# Revit family: 859-002X-001 DN350-600
name_source: partatom
category: Pipe Accessories
units: mm (PartAtom-declared; Revit-internal decimal feet)

## family parameters
Always vertical = Yes
Cut with Voids When Loaded = No
Part Type = Valve - Breaks Into
Round Connector Dimension = Use Diameter
Shared = No
Work Plane-Based = No

## types (40) — shared parameters
10 = 10 mm  [stored 0.0328084 ft]
18 = 11 mm  [stored 0.0360892 ft]
3 = 3 mm  [stored 0.00984252 ft]
50 = 50 mm
8 = 8 mm  [stored 0.0262467 ft]
DN350_PN10 Flow range ( 170 - 420) = 859-0350-00-0140020
DN350_PN10 Flow range ( 225 - 555) = 859-0350-00-0140021
DN350_PN10 Flow range ( 510 - 1250) = 859-0350-00-0140022
DN350_PN10 Flow range ( 650 - 1595) = 859-0350-00-0140023
DN350_PN16 Flow range ( 170 - 420) = 859-0350-00-1140020
DN350_PN16 Flow range ( 225 - 555) = 859-0350-00-1140021
859-0350-00-1140021
859-0350-00-1140021
859-0350-00-1140021
DN350_PN16 Flow range ( 510 - 1250) = 859-0350-00-1140022
DN350_PN16 Flow range ( 650 - 1595) = 859-0350-00-1140023
DN400_PN10 Flow range ( 225 - 545) = 859-0400-00-0140020
DN400_PN10 Flow range ( 370 - 905) = 859-0400-00-0140021
DN400_PN10 Flow range ( 525 - 1285) = 859-0400-00-0140022
DN400_PN10 Flow range ( 740 - 1815) = 859-0400-00-0140023
DN400_PN16 Flow range ( 225 - 545) = 859-0400-00-1140020
DN400_PN16 Flow range ( 370 - 905) = 859-0400-00-1140021
DN400_PN16 Flow range ( 525 - 1285) = 859-0400-00-1140022
DN400_PN16 Flow range ( 740 - 1815) = 859-0400-00-1140023
DN450_PN10 Flow range ( 1020 - 2495) = 859-0450-00-0140023
DN450_PN10 Flow range ( 280 - 690) = 859-0450-00-0140020
DN450_PN10 Flow range ( 445 - 1090) = 859-0450-00-0140021
DN450_PN10 Flow range ( 675 - 1640) = 859-0450-00-0140022
DN450_PN16 Flow range ( 1020 - 2495) = 859-0450-00-1140023
DN450_PN16 Flow range ( 280 - 690) = 859-0450-00-1140020
DN450_PN16 Flow range ( 445 - 1090) = 859-0450-00-1140021
DN450_PN16 Flow range ( 675 - 1640) = 859-0450-00-1140022
DN500_PN10 Flow range ( 1115 - 2715) = 859-0500-00-0140023
DN500_PN10 Flow range ( 350 - 835) = 859-0500-00-0140020
DN500_PN10 Flow range ( 530 - 1290) = 859-0500-00-0140021
DN500_PN10 Flow range ( 765 - 1860) = 859-0500-00-0140022
DN500_PN16 Flow range ( 1115 - 2715) = 859-0500-00-1140023
DN500_PN16 Flow range ( 350 - 835) = 859-0500-00-1140020
DN500_PN16 Flow range ( 530 - 1290) = 859-0500-00-1140021
DN500_PN16 Flow range ( 765 - 1860) = 859-0500-00-1140022
DN600_PN10 Flow range ( 1780 - 4350) = 859-0600-00-0140023
DN600_PN10 Flow range ( 500 - 1225) = 859-0600-00-0140020
DN600_PN10 Flow range ( 710 - 1735) = 859-0600-00-0140021
DN600_PN10 Flow range ( 970 - 2360) = 859-0600-00-0140022
DN600_PN16 Flow range ( 1780 - 4350) = 859-0600-00-1140023
DN600_PN16 Flow range ( 500 - 1225) = 859-0600-00-1140020
DN600_PN16 Flow range ( 710 - 1735) = 859-0600-00-1140021
DN600_PN16 Flow range ( 970 - 2360) = 859-0600-00-1140022
Description_ = AVK CONTROL VALVE, CONSTANT FLOW, PN10/16
Orifice_FL_T = 14 mm  [stored 0.0459318 ft]
Search_table = 859-002X-001 DN350-600
URL_product_pages = https://www.avkvalves.com
zero-valued in all types: 0, Default Elevation

## per-type parameters (varying)
- DN350_PN10 Flow range ( 170 - 420): Actuator_L=136 mm; Actuator_L1=122 mm; Actuator_d=41 mm; Body_H=312 mm; Body_Rib_L=130 mm; Bolt_Dia=33 mm; Bonnet_D=156 mm; Bonnet_D1=312 mm; Bonnet_R=328 mm; Bonnet_dim1=218 mm; Bonnet_dim1_H=32 mm; Bonnet_dim1_H1=431 mm; Bonnet_dim2=109 mm; Bonnet_dim3=82 mm; Bore=175 mm; Bore1=210 mm; Bore2=280 mm; Centre_D=90 mm; Centre_D1=72 mm; Centre_nut=68 mm; Control_dim1=16 mm  [stored 0.0524934 ft]; Control_dim2=98 mm; Control_dim3=8 mm  [stored 0.0262467 ft]; Control_dim4=281 mm; Control_dim5=22 mm; Control_dim6=27 mm; Control_dim7=48 mm; D=260 mm; DN=350 mm; FL_T=27 mm; H3=796 mm; H33=99 mm; H4=199 mm; L=980 mm; L3=360 mm; Nut_Dim1=42 mm; Nut_Dim2=7 mm  [stored 0.0229659 ft]; Nut_T=21 mm; Orifice_FL=219 mm; Raised_R=34 mm  [stored 0.111549 ft]; Raised_dis=4 mm  [stored 0.0131234 ft]; Sweep_R=19 mm  [stored 0.062336 ft]; Thickness=16 mm  [stored 0.0524934 ft]; Thickness1=19 mm  [stored 0.062336 ft]; Total_L=995 mm; W=290 mm; W1=302 mm; W11=208 mm; W2=302 mm; W22=242 mm; centre=273 mm; dim1=91 mm; nut_dim=156 mm; sweep=30 mm  [stored 0.0984252 ft]; sweep/2=6 mm  [stored 0.019685 ft]; sweep1=13 mm  [stored 0.0426509 ft]; sweep_D=25 mm  [stored 0.082021 ft]; sweep_H=375 mm; sweep_H1=44 mm; sweep_box1=36 mm  [stored 0.11811 ft]; sweep_box2=16 mm  [stored 0.0524934 ft]; w1=302 mm; w2=302 mm
- DN350_PN10 Flow range ( 225 - 555): Actuator_L=136 mm; Actuator_L1=122 mm; Actuator_d=41 mm; Body_H=312 mm; Body_Rib_L=130 mm; Bolt_Dia=33 mm; Bonnet_D=156 mm; Bonnet_D1=312 mm; Bonnet_R=328 mm; Bonnet_dim1=218 mm; Bonnet_dim1_H=32 mm; Bonnet_dim1_H1=431 mm; Bonnet_dim2=109 mm; Bonnet_dim3=82 mm; Bore=175 mm; Bore1=210 mm; Bore2=280 mm; Centre_D=90 mm; Centre_D1=72 mm; Centre_nut=68 mm; Control_dim1=16 mm  [stored 0.0524934 ft]; Control_dim2=98 mm; Control_dim3=8 mm  [stored 0.0262467 ft]; Control_dim4=281 mm; Control_dim5=22 mm; Control_dim6=27 mm; Control_dim7=48 mm; D=260 mm; DN=350 mm; FL_T=27 mm; H3=796 mm; H33=99 mm; H4=199 mm; L=980 mm; L3=360 mm; Nut_Dim1=42 mm; Nut_Dim2=7 mm  [stored 0.0229659 ft]; Nut_T=21 mm; Orifice_FL=219 mm; Raised_R=34 mm  [stored 0.111549 ft]; Raised_dis=4 mm  [stored 0.0131234 ft]; Sweep_R=19 mm  [stored 0.062336 ft]; Thickness=16 mm  [stored 0.0524934 ft]; Thickness1=19 mm  [stored 0.062336 ft]; Total_L=995 mm; W=290 mm; W1=302 mm; W11=208 mm; W2=302 mm; W22=242 mm; centre=273 mm; dim1=91 mm; nut_dim=156 mm; sweep=30 mm  [stored 0.0984252 ft]; sweep/2=6 mm  [stored 0.019685 ft]; sweep1=13 mm  [stored 0.0426509 ft]; sweep_D=25 mm  [stored 0.082021 ft]; sweep_H=375 mm; sweep_H1=44 mm; sweep_box1=36 mm  [stored 0.11811 ft]; sweep_box2=16 mm  [stored 0.0524934 ft]; w1=302 mm; w2=302 mm
- DN350_PN10 Flow range ( 510 - 1250): Actuator_L=136 mm; Actuator_L1=122 mm; Actuator_d=41 mm; Body_H=312 mm; Body_Rib_L=130 mm; Bolt_Dia=33 mm; Bonnet_D=156 mm; Bonnet_D1=312 mm; Bonnet_R=328 mm; Bonnet_dim1=218 mm; Bonnet_dim1_H=32 mm; Bonnet_dim1_H1=431 mm; Bonnet_dim2=109 mm; Bonnet_dim3=82 mm; Bore=175 mm; Bore1=210 mm; Bore2=280 mm; Centre_D=90 mm; Centre_D1=72 mm; Centre_nut=68 mm; Control_dim1=16 mm  [stored 0.0524934 ft]; Control_dim2=98 mm; Control_dim3=8 mm  [stored 0.0262467 ft]; Control_dim4=281 mm; Control_dim5=22 mm; Control_dim6=27 mm; Control_dim7=48 mm; D=260 mm; DN=350 mm; FL_T=27 mm; H3=796 mm; H33=99 mm; H4=199 mm; L=980 mm; L3=360 mm; Nut_Dim1=42 mm; Nut_Dim2=7 mm  [stored 0.0229659 ft]; Nut_T=21 mm; Orifice_FL=219 mm; Raised_R=34 mm  [stored 0.111549 ft]; Raised_dis=4 mm  [stored 0.0131234 ft]; Sweep_R=19 mm  [stored 0.062336 ft]; Thickness=16 mm  [stored 0.0524934 ft]; Thickness1=19 mm  [stored 0.062336 ft]; Total_L=995 mm; W=290 mm; W1=302 mm; W11=208 mm; W2=302 mm; W22=242 mm; centre=273 mm; dim1=91 mm; nut_dim=156 mm; sweep=30 mm  [stored 0.0984252 ft]; sweep/2=6 mm  [stored 0.019685 ft]; sweep1=13 mm  [stored 0.0426509 ft]; sweep_D=25 mm  [stored 0.082021 ft]; sweep_H=375 mm; sweep_H1=44 mm; sweep_box1=36 mm  [stored 0.11811 ft]; sweep_box2=16 mm  [stored 0.0524934 ft]; w1=302 mm; w2=302 mm
- DN350_PN10 Flow range ( 650 - 1595): Actuator_L=136 mm; Actuator_L1=122 mm; Actuator_d=41 mm; Body_H=312 mm; Body_Rib_L=130 mm; Bolt_Dia=33 mm; Bonnet_D=156 mm; Bonnet_D1=312 mm; Bonnet_R=328 mm; Bonnet_dim1=218 mm; Bonnet_dim1_H=32 mm; Bonnet_dim1_H1=431 mm; Bonnet_dim2=109 mm; Bonnet_dim3=82 mm; Bore=175 mm; Bore1=210 mm; Bore2=280 mm; Centre_D=90 mm; Centre_D1=72 mm; Centre_nut=68 mm; Control_dim1=16 mm  [stored 0.0524934 ft]; Control_dim2=98 mm; Control_dim3=8 mm  [stored 0.0262467 ft]; Control_dim4=281 mm; Control_dim5=22 mm; Control_dim6=27 mm; Control_dim7=48 mm; D=260 mm; DN=350 mm; FL_T=27 mm; H3=796 mm; H33=99 mm; H4=199 mm; L=980 mm; L3=360 mm; Nut_Dim1=42 mm; Nut_Dim2=7 mm  [stored 0.0229659 ft]; Nut_T=21 mm; Orifice_FL=219 mm; Raised_R=34 mm  [stored 0.111549 ft]; Raised_dis=4 mm  [stored 0.0131234 ft]; Sweep_R=19 mm  [stored 0.062336 ft]; Thickness=16 mm  [stored 0.0524934 ft]; Thickness1=19 mm  [stored 0.062336 ft]; Total_L=995 mm; W=290 mm; W1=302 mm; W11=208 mm; W2=302 mm; W22=242 mm; centre=273 mm; dim1=91 mm; nut_dim=156 mm; sweep=30 mm  [stored 0.0984252 ft]; sweep/2=6 mm  [stored 0.019685 ft]; sweep1=13 mm  [stored 0.0426509 ft]; sweep_D=25 mm  [stored 0.082021 ft]; sweep_H=375 mm; sweep_H1=44 mm; sweep_box1=36 mm  [stored 0.11811 ft]; sweep_box2=16 mm  [stored 0.0524934 ft]; w1=302 mm; w2=302 mm
- DN350_PN16 Flow range ( 170 - 420): Actuator_L=136 mm; Actuator_L1=122 mm; Actuator_d=41 mm; Body_H=312 mm; Body_Rib_L=130 mm; Bolt_Dia=33 mm; Bonnet_D=156 mm; Bonnet_D1=312 mm; Bonnet_R=328 mm; Bonnet_dim1=218 mm; Bonnet_dim1_H=32 mm; Bonnet_dim1_H1=431 mm; Bonnet_dim2=109 mm; Bonnet_dim3=82 mm; Bore=175 mm; Bore1=210 mm; Bore2=280 mm; Centre_D=90 mm; Centre_D1=72 mm; Centre_nut=68 mm; Control_dim1=16 mm  [stored 0.0524934 ft]; Control_dim2=98 mm; Control_dim3=8 mm  [stored 0.0262467 ft]; Control_dim4=281 mm; Control_dim5=22 mm; Control_dim6=27 mm; Control_dim7=48 mm; D=260 mm; DN=350 mm; FL_T=27 mm; H3=796 mm; H33=99 mm; H4=199 mm; L=980 mm; L3=360 mm; Nut_Dim1=42 mm; Nut_Dim2=7 mm  [stored 0.0229659 ft]; Nut_T=21 mm; Orifice_FL=219 mm; Raised_R=34 mm  [stored 0.111549 ft]; Raised_dis=4 mm  [stored 0.0131234 ft]; Sweep_R=19 mm  [stored 0.062336 ft]; Thickness=16 mm  [stored 0.0524934 ft]; Thickness1=19 mm  [stored 0.062336 ft]; Total_L=995 mm; W=290 mm; W1=302 mm; W11=208 mm; W2=302 mm; W22=242 mm; centre=273 mm; dim1=91 mm; nut_dim=156 mm; sweep=30 mm  [stored 0.0984252 ft]; sweep/2=6 mm  [stored 0.019685 ft]; sweep1=13 mm  [stored 0.0426509 ft]; sweep_D=25 mm  [stored 0.082021 ft]; sweep_H=375 mm; sweep_H1=44 mm; sweep_box1=36 mm  [stored 0.11811 ft]; sweep_box2=16 mm  [stored 0.0524934 ft]; w1=302 mm; w2=302 mm
- DN350_PN16 Flow range ( 225 - 555): Actuator_L=136 mm; Actuator_L1=122 mm; Actuator_d=41 mm; Body_H=312 mm; Body_Rib_L=130 mm; Bolt_Dia=33 mm; Bonnet_D=156 mm; Bonnet_D1=312 mm; Bonnet_R=328 mm; Bonnet_dim1=218 mm; Bonnet_dim1_H=32 mm; Bonnet_dim1_H1=431 mm; Bonnet_dim2=109 mm; Bonnet_dim3=82 mm; Bore=175 mm; Bore1=210 mm; Bore2=280 mm; Centre_D=90 mm; Centre_D1=72 mm; Centre_nut=68 mm; Control_dim1=16 mm  [stored 0.0524934 ft]; Control_dim2=98 mm; Control_dim3=8 mm  [stored 0.0262467 ft]; Control_dim4=281 mm; Control_dim5=22 mm; Control_dim6=27 mm; Control_dim7=48 mm; D=260 mm; DN=350 mm; FL_T=27 mm; H3=796 mm; H33=99 mm; H4=199 mm; L=980 mm; L3=360 mm; Nut_Dim1=42 mm; Nut_Dim2=7 mm  [stored 0.0229659 ft]; Nut_T=21 mm; Orifice_FL=219 mm; Raised_R=34 mm  [stored 0.111549 ft]; Raised_dis=4 mm  [stored 0.0131234 ft]; Sweep_R=19 mm  [stored 0.062336 ft]; Thickness=16 mm  [stored 0.0524934 ft]; Thickness1=19 mm  [stored 0.062336 ft]; Total_L=995 mm; W=290 mm; W1=302 mm; W11=208 mm; W2=302 mm; W22=242 mm; centre=273 mm; dim1=91 mm; nut_dim=156 mm; sweep=30 mm  [stored 0.0984252 ft]; sweep/2=6 mm  [stored 0.019685 ft]; sweep1=13 mm  [stored 0.0426509 ft]; sweep_D=25 mm  [stored 0.082021 ft]; sweep_H=375 mm; sweep_H1=44 mm; sweep_box1=36 mm  [stored 0.11811 ft]; sweep_box2=16 mm  [stored 0.0524934 ft]; w1=302 mm; w2=302 mm
- DN350_PN16 Flow range ( 510 - 1250): Actuator_L=136 mm; Actuator_L1=122 mm; Actuator_d=41 mm; Body_H=312 mm; Body_Rib_L=130 mm; Bolt_Dia=33 mm; Bonnet_D=156 mm; Bonnet_D1=312 mm; Bonnet_R=328 mm; Bonnet_dim1=218 mm; Bonnet_dim1_H=32 mm; Bonnet_dim1_H1=431 mm; Bonnet_dim2=109 mm; Bonnet_dim3=82 mm; Bore=175 mm; Bore1=210 mm; Bore2=280 mm; Centre_D=90 mm; Centre_D1=72 mm; Centre_nut=68 mm; Control_dim1=16 mm  [stored 0.0524934 ft]; Control_dim2=98 mm; Control_dim3=8 mm  [stored 0.0262467 ft]; Control_dim4=281 mm; Control_dim5=22 mm; Control_dim6=27 mm; Control_dim7=48 mm; D=260 mm; DN=350 mm; FL_T=27 mm; H3=796 mm; H33=99 mm; H4=199 mm; L=980 mm; L3=360 mm; Nut_Dim1=42 mm; Nut_Dim2=7 mm  [stored 0.0229659 ft]; Nut_T=21 mm; Orifice_FL=219 mm; Raised_R=34 mm  [stored 0.111549 ft]; Raised_dis=4 mm  [stored 0.0131234 ft]; Sweep_R=19 mm  [stored 0.062336 ft]; Thickness=16 mm  [stored 0.0524934 ft]; Thickness1=19 mm  [stored 0.062336 ft]; Total_L=995 mm; W=290 mm; W1=302 mm; W11=208 mm; W2=302 mm; W22=242 mm; centre=273 mm; dim1=91 mm; nut_dim=156 mm; sweep=30 mm  [stored 0.0984252 ft]; sweep/2=6 mm  [stored 0.019685 ft]; sweep1=13 mm  [stored 0.0426509 ft]; sweep_D=25 mm  [stored 0.082021 ft]; sweep_H=375 mm; sweep_H1=44 mm; sweep_box1=36 mm  [stored 0.11811 ft]; sweep_box2=16 mm  [stored 0.0524934 ft]; w1=302 mm; w2=302 mm
- DN350_PN16 Flow range ( 650 - 1595): Actuator_L=136 mm; Actuator_L1=122 mm; Actuator_d=41 mm; Body_H=312 mm; Body_Rib_L=130 mm; Bolt_Dia=33 mm; Bonnet_D=156 mm; Bonnet_D1=312 mm; Bonnet_R=328 mm; Bonnet_dim1=218 mm; Bonnet_dim1_H=32 mm; Bonnet_dim1_H1=431 mm; Bonnet_dim2=109 mm; Bonnet_dim3=82 mm; Bore=175 mm; Bore1=210 mm; Bore2=280 mm; Centre_D=90 mm; Centre_D1=72 mm; Centre_nut=68 mm; Control_dim1=16 mm  [stored 0.0524934 ft]; Control_dim2=98 mm; Control_dim3=8 mm  [stored 0.0262467 ft]; Control_dim4=281 mm; Control_dim5=22 mm; Control_dim6=27 mm; Control_dim7=48 mm; D=260 mm; DN=350 mm; FL_T=27 mm; H3=796 mm; H33=99 mm; H4=199 mm; L=980 mm; L3=360 mm; Nut_Dim1=42 mm; Nut_Dim2=7 mm  [stored 0.0229659 ft]; Nut_T=21 mm; Orifice_FL=219 mm; Raised_R=34 mm  [stored 0.111549 ft]; Raised_dis=4 mm  [stored 0.0131234 ft]; Sweep_R=19 mm  [stored 0.062336 ft]; Thickness=16 mm  [stored 0.0524934 ft]; Thickness1=19 mm  [stored 0.062336 ft]; Total_L=995 mm; W=290 mm; W1=302 mm; W11=208 mm; W2=302 mm; W22=242 mm; centre=273 mm; dim1=91 mm; nut_dim=156 mm; sweep=30 mm  [stored 0.0984252 ft]; sweep/2=6 mm  [stored 0.019685 ft]; sweep1=13 mm  [stored 0.0426509 ft]; sweep_D=25 mm  [stored 0.082021 ft]; sweep_H=375 mm; sweep_H1=44 mm; sweep_box1=36 mm  [stored 0.11811 ft]; sweep_box2=16 mm  [stored 0.0524934 ft]; w1=302 mm; w2=302 mm
- DN400_PN10 Flow range ( 225 - 545): Actuator_L=160 mm; Actuator_L1=144 mm; Actuator_d=45 mm  [stored 0.147638 ft]; Body_H=348 mm; Body_Rib_L=145 mm; Bolt_Dia=39 mm  [stored 0.127953 ft]; Bonnet_D=174 mm; Bonnet_D1=348 mm; Bonnet_R=365 mm; Bonnet_dim1=244 mm; Bonnet_dim1_H=47 mm; Bonnet_dim1_H1=507 mm; Bonnet_dim2=122 mm; Bonnet_dim3=91 mm; Bore=200 mm; Bore1=240 mm; Bore2=320 mm; Centre_D=90 mm; Centre_D1=72 mm; Centre_nut=68 mm; Control_dim1=18 mm  [stored 0.0590551 ft]; Control_dim2=110 mm; Control_dim3=9 mm  [stored 0.0295276 ft]; Control_dim4=313 mm; Control_dim5=25 mm  [stored 0.082021 ft]; Control_dim6=30 mm  [stored 0.0984252 ft]; Control_dim7=53 mm; D=290 mm; DN=400 mm; FL_T=28 mm  [stored 0.0918635 ft]; H3=920 mm; H33=117 mm; H4=233 mm; L=1100 mm; L3=402 mm; Nut_Dim1=51 mm; Nut_Dim2=7 mm  [stored 0.0229659 ft]; Nut_T=22 mm; Orifice_FL=244 mm; Raised_R=36 mm  [stored 0.11811 ft]; Raised_dis=4 mm  [stored 0.0131234 ft]; Sweep_R=23 mm; Thickness=17 mm; Thickness1=20 mm  [stored 0.0656168 ft]; Total_L=1115 mm; W=340 mm; W1=355 mm; W11=244 mm; W2=355 mm; W22=284 mm; centre=312 mm; dim1=107 mm; nut_dim=174 mm; sweep=36 mm  [stored 0.11811 ft]; sweep/2=8 mm  [stored 0.0262467 ft]; sweep1=15 mm  [stored 0.0492126 ft]; sweep_D=30 mm  [stored 0.0984252 ft]; sweep_H=441 mm; sweep_H1=65 mm; sweep_box1=36 mm  [stored 0.11811 ft]; sweep_box2=20 mm  [stored 0.0656168 ft]; w1=355 mm; w2=355 mm
- DN400_PN10 Flow range ( 370 - 905): Actuator_L=160 mm; Actuator_L1=144 mm; Actuator_d=45 mm  [stored 0.147638 ft]; Body_H=348 mm; Body_Rib_L=145 mm; Bolt_Dia=39 mm  [stored 0.127953 ft]; Bonnet_D=174 mm; Bonnet_D1=348 mm; Bonnet_R=365 mm; Bonnet_dim1=244 mm; Bonnet_dim1_H=47 mm; Bonnet_dim1_H1=507 mm; Bonnet_dim2=122 mm; Bonnet_dim3=91 mm; Bore=200 mm; Bore1=240 mm; Bore2=320 mm; Centre_D=90 mm; Centre_D1=72 mm; Centre_nut=68 mm; Control_dim1=18 mm  [stored 0.0590551 ft]; Control_dim2=110 mm; Control_dim3=9 mm  [stored 0.0295276 ft]; Control_dim4=313 mm; Control_dim5=25 mm  [stored 0.082021 ft]; Control_dim6=30 mm  [stored 0.0984252 ft]; Control_dim7=53 mm; D=290 mm; DN=400 mm; FL_T=28 mm  [stored 0.0918635 ft]; H3=920 mm; H33=117 mm; H4=233 mm; L=1100 mm; L3=402 mm; Nut_Dim1=51 mm; Nut_Dim2=7 mm  [stored 0.0229659 ft]; Nut_T=22 mm; Orifice_FL=244 mm; Raised_R=36 mm  [stored 0.11811 ft]; Raised_dis=4 mm  [stored 0.0131234 ft]; Sweep_R=23 mm; Thickness=17 mm; Thickness1=20 mm  [stored 0.0656168 ft]; Total_L=1115 mm; W=340 mm; W1=355 mm; W11=244 mm; W2=355 mm; W22=284 mm; centre=312 mm; dim1=107 mm; nut_dim=174 mm; sweep=36 mm  [stored 0.11811 ft]; sweep/2=8 mm  [stored 0.0262467 ft]; sweep1=15 mm  [stored 0.0492126 ft]; sweep_D=30 mm  [stored 0.0984252 ft]; sweep_H=441 mm; sweep_H1=65 mm; sweep_box1=36 mm  [stored 0.11811 ft]; sweep_box2=20 mm  [stored 0.0656168 ft]; w1=355 mm; w2=355 mm
- DN400_PN10 Flow range ( 525 - 1285): Actuator_L=160 mm; Actuator_L1=144 mm; Actuator_d=45 mm  [stored 0.147638 ft]; Body_H=348 mm; Body_Rib_L=145 mm; Bolt_Dia=39 mm  [stored 0.127953 ft]; Bonnet_D=174 mm; Bonnet_D1=348 mm; Bonnet_R=365 mm; Bonnet_dim1=244 mm; Bonnet_dim1_H=47 mm; Bonnet_dim1_H1=507 mm; Bonnet_dim2=122 mm; Bonnet_dim3=91 mm; Bore=200 mm; Bore1=240 mm; Bore2=320 mm; Centre_D=90 mm; Centre_D1=72 mm; Centre_nut=68 mm; Control_dim1=18 mm  [stored 0.0590551 ft]; Control_dim2=110 mm; Control_dim3=9 mm  [stored 0.0295276 ft]; Control_dim4=313 mm; Control_dim5=25 mm  [stored 0.082021 ft]; Control_dim6=30 mm  [stored 0.0984252 ft]; Control_dim7=53 mm; D=290 mm; DN=400 mm; FL_T=28 mm  [stored 0.0918635 ft]; H3=920 mm; H33=117 mm; H4=233 mm; L=1100 mm; L3=402 mm; Nut_Dim1=51 mm; Nut_Dim2=7 mm  [stored 0.0229659 ft]; Nut_T=22 mm; Orifice_FL=244 mm; Raised_R=36 mm  [stored 0.11811 ft]; Raised_dis=4 mm  [stored 0.0131234 ft]; Sweep_R=23 mm; Thickness=17 mm; Thickness1=20 mm  [stored 0.0656168 ft]; Total_L=1115 mm; W=340 mm; W1=355 mm; W11=244 mm; W2=355 mm; W22=284 mm; centre=312 mm; dim1=107 mm; nut_dim=174 mm; sweep=36 mm  [stored 0.11811 ft]; sweep/2=8 mm  [stored 0.0262467 ft]; sweep1=15 mm  [stored 0.0492126 ft]; sweep_D=30 mm  [stored 0.0984252 ft]; sweep_H=441 mm; sweep_H1=65 mm; sweep_box1=36 mm  [stored 0.11811 ft]; sweep_box2=20 mm  [stored 0.0656168 ft]; w1=355 mm; w2=355 mm
- DN400_PN10 Flow range ( 740 - 1815): Actuator_L=160 mm; Actuator_L1=144 mm; Actuator_d=45 mm  [stored 0.147638 ft]; Body_H=348 mm; Body_Rib_L=145 mm; Bolt_Dia=39 mm  [stored 0.127953 ft]; Bonnet_D=174 mm; Bonnet_D1=348 mm; Bonnet_R=365 mm; Bonnet_dim1=244 mm; Bonnet_dim1_H=47 mm; Bonnet_dim1_H1=507 mm; Bonnet_dim2=122 mm; Bonnet_dim3=91 mm; Bore=200 mm; Bore1=240 mm; Bore2=320 mm; Centre_D=90 mm; Centre_D1=72 mm; Centre_nut=68 mm; Control_dim1=18 mm  [stored 0.0590551 ft]; Control_dim2=110 mm; Control_dim3=9 mm  [stored 0.0295276 ft]; Control_dim4=313 mm; Control_dim5=25 mm  [stored 0.082021 ft]; Control_dim6=30 mm  [stored 0.0984252 ft]; Control_dim7=53 mm; D=290 mm; DN=400 mm; FL_T=28 mm  [stored 0.0918635 ft]; H3=920 mm; H33=117 mm; H4=233 mm; L=1100 mm; L3=402 mm; Nut_Dim1=51 mm; Nut_Dim2=7 mm  [stored 0.0229659 ft]; Nut_T=22 mm; Orifice_FL=244 mm; Raised_R=36 mm  [stored 0.11811 ft]; Raised_dis=4 mm  [stored 0.0131234 ft]; Sweep_R=23 mm; Thickness=17 mm; Thickness1=20 mm  [stored 0.0656168 ft]; Total_L=1115 mm; W=340 mm; W1=355 mm; W11=244 mm; W2=355 mm; W22=284 mm; centre=312 mm; dim1=107 mm; nut_dim=174 mm; sweep=36 mm  [stored 0.11811 ft]; sweep/2=8 mm  [stored 0.0262467 ft]; sweep1=15 mm  [stored 0.0492126 ft]; sweep_D=30 mm  [stored 0.0984252 ft]; sweep_H=441 mm; sweep_H1=65 mm; sweep_box1=36 mm  [stored 0.11811 ft]; sweep_box2=20 mm  [stored 0.0656168 ft]; w1=355 mm; w2=355 mm
- DN400_PN16 Flow range ( 225 - 545): Actuator_L=160 mm; Actuator_L1=144 mm; Actuator_d=45 mm  [stored 0.147638 ft]; Body_H=348 mm; Body_Rib_L=145 mm; Bolt_Dia=39 mm  [stored 0.127953 ft]; Bonnet_D=174 mm; Bonnet_D1=348 mm; Bonnet_R=365 mm; Bonnet_dim1=244 mm; Bonnet_dim1_H=47 mm; Bonnet_dim1_H1=507 mm; Bonnet_dim2=122 mm; Bonnet_dim3=91 mm; Bore=200 mm; Bore1=240 mm; Bore2=320 mm; Centre_D=90 mm; Centre_D1=72 mm; Centre_nut=68 mm; Control_dim1=18 mm  [stored 0.0590551 ft]; Control_dim2=110 mm; Control_dim3=9 mm  [stored 0.0295276 ft]; Control_dim4=313 mm; Control_dim5=25 mm  [stored 0.082021 ft]; Control_dim6=30 mm  [stored 0.0984252 ft]; Control_dim7=53 mm; D=290 mm; DN=400 mm; FL_T=28 mm  [stored 0.0918635 ft]; H3=920 mm; H33=117 mm; H4=233 mm; L=1100 mm; L3=402 mm; Nut_Dim1=51 mm; Nut_Dim2=7 mm  [stored 0.0229659 ft]; Nut_T=22 mm; Orifice_FL=244 mm; Raised_R=36 mm  [stored 0.11811 ft]; Raised_dis=4 mm  [stored 0.0131234 ft]; Sweep_R=23 mm; Thickness=17 mm; Thickness1=20 mm  [stored 0.0656168 ft]; Total_L=1115 mm; W=340 mm; W1=355 mm; W11=244 mm; W2=355 mm; W22=284 mm; centre=312 mm; dim1=107 mm; nut_dim=174 mm; sweep=36 mm  [stored 0.11811 ft]; sweep/2=8 mm  [stored 0.0262467 ft]; sweep1=15 mm  [stored 0.0492126 ft]; sweep_D=30 mm  [stored 0.0984252 ft]; sweep_H=441 mm; sweep_H1=65 mm; sweep_box1=36 mm  [stored 0.11811 ft]; sweep_box2=20 mm  [stored 0.0656168 ft]; w1=355 mm; w2=355 mm
- DN400_PN16 Flow range ( 370 - 905): Actuator_L=160 mm; Actuator_L1=144 mm; Actuator_d=45 mm  [stored 0.147638 ft]; Body_H=348 mm; Body_Rib_L=145 mm; Bolt_Dia=39 mm  [stored 0.127953 ft]; Bonnet_D=174 mm; Bonnet_D1=348 mm; Bonnet_R=365 mm; Bonnet_dim1=244 mm; Bonnet_dim1_H=47 mm; Bonnet_dim1_H1=507 mm; Bonnet_dim2=122 mm; Bonnet_dim3=91 mm; Bore=200 mm; Bore1=240 mm; Bore2=320 mm; Centre_D=90 mm; Centre_D1=72 mm; Centre_nut=68 mm; Control_dim1=18 mm  [stored 0.0590551 ft]; Control_dim2=110 mm; Control_dim3=9 mm  [stored 0.0295276 ft]; Control_dim4=313 mm; Control_dim5=25 mm  [stored 0.082021 ft]; Control_dim6=30 mm  [stored 0.0984252 ft]; Control_dim7=53 mm; D=290 mm; DN=400 mm; FL_T=28 mm  [stored 0.0918635 ft]; H3=920 mm; H33=117 mm; H4=233 mm; L=1100 mm; L3=402 mm; Nut_Dim1=51 mm; Nut_Dim2=7 mm  [stored 0.0229659 ft]; Nut_T=22 mm; Orifice_FL=244 mm; Raised_R=36 mm  [stored 0.11811 ft]; Raised_dis=4 mm  [stored 0.0131234 ft]; Sweep_R=23 mm; Thickness=17 mm; Thickness1=20 mm  [stored 0.0656168 ft]; Total_L=1115 mm; W=340 mm; W1=355 mm; W11=244 mm; W2=355 mm; W22=284 mm; centre=312 mm; dim1=107 mm; nut_dim=174 mm; sweep=36 mm  [stored 0.11811 ft]; sweep/2=8 mm  [stored 0.0262467 ft]; sweep1=15 mm  [stored 0.0492126 ft]; sweep_D=30 mm  [stored 0.0984252 ft]; sweep_H=441 mm; sweep_H1=65 mm; sweep_box1=36 mm  [stored 0.11811 ft]; sweep_box2=20 mm  [stored 0.0656168 ft]; w1=355 mm; w2=355 mm
- DN400_PN16 Flow range ( 525 - 1285): Actuator_L=160 mm; Actuator_L1=144 mm; Actuator_d=45 mm  [stored 0.147638 ft]; Body_H=348 mm; Body_Rib_L=145 mm; Bolt_Dia=39 mm  [stored 0.127953 ft]; Bonnet_D=174 mm; Bonnet_D1=348 mm; Bonnet_R=365 mm; Bonnet_dim1=244 mm; Bonnet_dim1_H=47 mm; Bonnet_dim1_H1=507 mm; Bonnet_dim2=122 mm; Bonnet_dim3=91 mm; Bore=200 mm; Bore1=240 mm; Bore2=320 mm; Centre_D=90 mm; Centre_D1=72 mm; Centre_nut=68 mm; Control_dim1=18 mm  [stored 0.0590551 ft]; Control_dim2=110 mm; Control_dim3=9 mm  [stored 0.0295276 ft]; Control_dim4=313 mm; Control_dim5=25 mm  [stored 0.082021 ft]; Control_dim6=30 mm  [stored 0.0984252 ft]; Control_dim7=53 mm; D=290 mm; DN=400 mm; FL_T=28 mm  [stored 0.0918635 ft]; H3=920 mm; H33=117 mm; H4=233 mm; L=1100 mm; L3=402 mm; Nut_Dim1=51 mm; Nut_Dim2=7 mm  [stored 0.0229659 ft]; Nut_T=22 mm; Orifice_FL=244 mm; Raised_R=36 mm  [stored 0.11811 ft]; Raised_dis=4 mm  [stored 0.0131234 ft]; Sweep_R=23 mm; Thickness=17 mm; Thickness1=20 mm  [stored 0.0656168 ft]; Total_L=1115 mm; W=340 mm; W1=355 mm; W11=244 mm; W2=355 mm; W22=284 mm; centre=312 mm; dim1=107 mm; nut_dim=174 mm; sweep=36 mm  [stored 0.11811 ft]; sweep/2=8 mm  [stored 0.0262467 ft]; sweep1=15 mm  [stored 0.0492126 ft]; sweep_D=30 mm  [stored 0.0984252 ft]; sweep_H=441 mm; sweep_H1=65 mm; sweep_box1=36 mm  [stored 0.11811 ft]; sweep_box2=20 mm  [stored 0.0656168 ft]; w1=355 mm; w2=355 mm
- DN400_PN16 Flow range ( 740 - 1815): Actuator_L=160 mm; Actuator_L1=144 mm; Actuator_d=45 mm  [stored 0.147638 ft]; Body_H=348 mm; Body_Rib_L=145 mm; Bolt_Dia=39 mm  [stored 0.127953 ft]; Bonnet_D=174 mm; Bonnet_D1=348 mm; Bonnet_R=365 mm; Bonnet_dim1=244 mm; Bonnet_dim1_H=47 mm; Bonnet_dim1_H1=507 mm; Bonnet_dim2=122 mm; Bonnet_dim3=91 mm; Bore=200 mm; Bore1=240 mm; Bore2=320 mm; Centre_D=90 mm; Centre_D1=72 mm; Centre_nut=68 mm; Control_dim1=18 mm  [stored 0.0590551 ft]; Control_dim2=110 mm; Control_dim3=9 mm  [stored 0.0295276 ft]; Control_dim4=313 mm; Control_dim5=25 mm  [stored 0.082021 ft]; Control_dim6=30 mm  [stored 0.0984252 ft]; Control_dim7=53 mm; D=290 mm; DN=400 mm; FL_T=28 mm  [stored 0.0918635 ft]; H3=920 mm; H33=117 mm; H4=233 mm; L=1100 mm; L3=402 mm; Nut_Dim1=51 mm; Nut_Dim2=7 mm  [stored 0.0229659 ft]; Nut_T=22 mm; Orifice_FL=244 mm; Raised_R=36 mm  [stored 0.11811 ft]; Raised_dis=4 mm  [stored 0.0131234 ft]; Sweep_R=23 mm; Thickness=17 mm; Thickness1=20 mm  [stored 0.0656168 ft]; Total_L=1115 mm; W=340 mm; W1=355 mm; W11=244 mm; W2=355 mm; W22=284 mm; centre=312 mm; dim1=107 mm; nut_dim=174 mm; sweep=36 mm  [stored 0.11811 ft]; sweep/2=8 mm  [stored 0.0262467 ft]; sweep1=15 mm  [stored 0.0492126 ft]; sweep_D=30 mm  [stored 0.0984252 ft]; sweep_H=441 mm; sweep_H1=65 mm; sweep_box1=36 mm  [stored 0.11811 ft]; sweep_box2=20 mm  [stored 0.0656168 ft]; w1=355 mm; w2=355 mm
- DN450_PN10 Flow range ( 280 - 690): Actuator_L=179 mm; Actuator_L1=161 mm; Actuator_d=50 mm; Body_H=384 mm; Body_Rib_L=160 mm; Bolt_Dia=39 mm  [stored 0.127953 ft]; Bonnet_D=192 mm; Bonnet_D1=384 mm; Bonnet_R=403 mm; Bonnet_dim1=269 mm; Bonnet_dim1_H=41 mm; Bonnet_dim1_H1=536 mm; Bonnet_dim2=134 mm; Bonnet_dim3=101 mm; Bore=225 mm; Bore1=270 mm; Bore2=360 mm; Centre_D=90 mm; Centre_D1=72 mm; Centre_nut=68 mm; Control_dim1=20 mm  [stored 0.0656168 ft]; Control_dim2=121 mm; Control_dim3=10 mm  [stored 0.0328084 ft]; Control_dim4=346 mm; Control_dim5=27 mm; Control_dim6=33 mm; Control_dim7=59 mm; D=320 mm; DN=450 mm; FL_T=30 mm  [stored 0.0984252 ft]; H3=986 mm; H33=123 mm; H4=247 mm; L=1200 mm; L3=444 mm; Nut_Dim1=51 mm; Nut_Dim2=8 mm  [stored 0.0262467 ft]; Nut_T=24 mm  [stored 0.0787402 ft]; Orifice_FL=269 mm; Raised_R=38 mm; Raised_dis=4 mm  [stored 0.0131234 ft]; Sweep_R=23 mm; Thickness=18 mm  [stored 0.0590551 ft]; Thickness1=22 mm; Total_L=1215 mm; W=383 mm; W1=398 mm; W11=276 mm; W2=398 mm; W22=318 mm; centre=351 mm; dim1=119 mm; nut_dim=192 mm; sweep=36 mm  [stored 0.11811 ft]; sweep/2=8 mm  [stored 0.0262467 ft]; sweep1=15 mm  [stored 0.0492126 ft]; sweep_D=30 mm  [stored 0.0984252 ft]; sweep_H=466 mm; sweep_H1=58 mm; sweep_box1=36 mm  [stored 0.11811 ft]; sweep_box2=20 mm  [stored 0.0656168 ft]; w1=398 mm; w2=398 mm
- DN450_PN10 Flow range ( 445 - 1090): Actuator_L=179 mm; Actuator_L1=161 mm; Actuator_d=50 mm; Body_H=384 mm; Body_Rib_L=160 mm; Bolt_Dia=39 mm  [stored 0.127953 ft]; Bonnet_D=192 mm; Bonnet_D1=384 mm; Bonnet_R=403 mm; Bonnet_dim1=269 mm; Bonnet_dim1_H=41 mm; Bonnet_dim1_H1=536 mm; Bonnet_dim2=134 mm; Bonnet_dim3=101 mm; Bore=225 mm; Bore1=270 mm; Bore2=360 mm; Centre_D=90 mm; Centre_D1=72 mm; Centre_nut=68 mm; Control_dim1=20 mm  [stored 0.0656168 ft]; Control_dim2=121 mm; Control_dim3=10 mm  [stored 0.0328084 ft]; Control_dim4=346 mm; Control_dim5=27 mm; Control_dim6=33 mm; Control_dim7=59 mm; D=320 mm; DN=450 mm; FL_T=30 mm  [stored 0.0984252 ft]; H3=986 mm; H33=123 mm; H4=247 mm; L=1200 mm; L3=444 mm; Nut_Dim1=51 mm; Nut_Dim2=8 mm  [stored 0.0262467 ft]; Nut_T=24 mm  [stored 0.0787402 ft]; Orifice_FL=269 mm; Raised_R=38 mm; Raised_dis=4 mm  [stored 0.0131234 ft]; Sweep_R=23 mm; Thickness=18 mm  [stored 0.0590551 ft]; Thickness1=22 mm; Total_L=1215 mm; W=383 mm; W1=398 mm; W11=276 mm; W2=398 mm; W22=318 mm; centre=351 mm; dim1=119 mm; nut_dim=192 mm; sweep=36 mm  [stored 0.11811 ft]; sweep/2=8 mm  [stored 0.0262467 ft]; sweep1=15 mm  [stored 0.0492126 ft]; sweep_D=30 mm  [stored 0.0984252 ft]; sweep_H=466 mm; sweep_H1=58 mm; sweep_box1=36 mm  [stored 0.11811 ft]; sweep_box2=20 mm  [stored 0.0656168 ft]; w1=398 mm; w2=398 mm
- DN450_PN10 Flow range ( 675 - 1640): Actuator_L=179 mm; Actuator_L1=161 mm; Actuator_d=50 mm; Body_H=384 mm; Body_Rib_L=160 mm; Bolt_Dia=39 mm  [stored 0.127953 ft]; Bonnet_D=192 mm; Bonnet_D1=384 mm; Bonnet_R=403 mm; Bonnet_dim1=269 mm; Bonnet_dim1_H=41 mm; Bonnet_dim1_H1=536 mm; Bonnet_dim2=134 mm; Bonnet_dim3=101 mm; Bore=225 mm; Bore1=270 mm; Bore2=360 mm; Centre_D=90 mm; Centre_D1=72 mm; Centre_nut=68 mm; Control_dim1=20 mm  [stored 0.0656168 ft]; Control_dim2=121 mm; Control_dim3=10 mm  [stored 0.0328084 ft]; Control_dim4=346 mm; Control_dim5=27 mm; Control_dim6=33 mm; Control_dim7=59 mm; D=320 mm; DN=450 mm; FL_T=30 mm  [stored 0.0984252 ft]; H3=986 mm; H33=123 mm; H4=247 mm; L=1200 mm; L3=444 mm; Nut_Dim1=51 mm; Nut_Dim2=8 mm  [stored 0.0262467 ft]; Nut_T=24 mm  [stored 0.0787402 ft]; Orifice_FL=269 mm; Raised_R=38 mm; Raised_dis=4 mm  [stored 0.0131234 ft]; Sweep_R=23 mm; Thickness=18 mm  [stored 0.0590551 ft]; Thickness1=22 mm; Total_L=1215 mm; W=383 mm; W1=398 mm; W11=276 mm; W2=398 mm; W22=318 mm; centre=351 mm; dim1=119 mm; nut_dim=192 mm; sweep=36 mm  [stored 0.11811 ft]; sweep/2=8 mm  [stored 0.0262467 ft]; sweep1=15 mm  [stored 0.0492126 ft]; sweep_D=30 mm  [stored 0.0984252 ft]; sweep_H=466 mm; sweep_H1=58 mm; sweep_box1=36 mm  [stored 0.11811 ft]; sweep_box2=20 mm  [stored 0.0656168 ft]; w1=398 mm; w2=398 mm
- DN450_PN10 Flow range ( 1020 - 2495): Actuator_L=179 mm; Actuator_L1=161 mm; Actuator_d=50 mm; Body_H=384 mm; Body_Rib_L=160 mm; Bolt_Dia=39 mm  [stored 0.127953 ft]; Bonnet_D=192 mm; Bonnet_D1=384 mm; Bonnet_R=403 mm; Bonnet_dim1=269 mm; Bonnet_dim1_H=41 mm; Bonnet_dim1_H1=536 mm; Bonnet_dim2=134 mm; Bonnet_dim3=101 mm; Bore=225 mm; Bore1=270 mm; Bore2=360 mm; Centre_D=90 mm; Centre_D1=72 mm; Centre_nut=68 mm; Control_dim1=20 mm  [stored 0.0656168 ft]; Control_dim2=121 mm; Control_dim3=10 mm  [stored 0.0328084 ft]; Control_dim4=346 mm; Control_dim5=27 mm; Control_dim6=33 mm; Control_dim7=59 mm; D=320 mm; DN=450 mm; FL_T=30 mm  [stored 0.0984252 ft]; H3=986 mm; H33=123 mm; H4=247 mm; L=1200 mm; L3=444 mm; Nut_Dim1=51 mm; Nut_Dim2=8 mm  [stored 0.0262467 ft]; Nut_T=24 mm  [stored 0.0787402 ft]; Orifice_FL=269 mm; Raised_R=38 mm; Raised_dis=4 mm  [stored 0.0131234 ft]; Sweep_R=23 mm; Thickness=18 mm  [stored 0.0590551 ft]; Thickness1=22 mm; Total_L=1215 mm; W=383 mm; W1=398 mm; W11=276 mm; W2=398 mm; W22=318 mm; centre=351 mm; dim1=119 mm; nut_dim=192 mm; sweep=36 mm  [stored 0.11811 ft]; sweep/2=8 mm  [stored 0.0262467 ft]; sweep1=15 mm  [stored 0.0492126 ft]; sweep_D=30 mm  [stored 0.0984252 ft]; sweep_H=466 mm; sweep_H1=58 mm; sweep_box1=36 mm  [stored 0.11811 ft]; sweep_box2=20 mm  [stored 0.0656168 ft]; w1=398 mm; w2=398 mm
- DN450_PN16 Flow range ( 280 - 690): Actuator_L=179 mm; Actuator_L1=161 mm; Actuator_d=50 mm; Body_H=384 mm; Body_Rib_L=160 mm; Bolt_Dia=39 mm  [stored 0.127953 ft]; Bonnet_D=192 mm; Bonnet_D1=384 mm; Bonnet_R=403 mm; Bonnet_dim1=269 mm; Bonnet_dim1_H=41 mm; Bonnet_dim1_H1=536 mm; Bonnet_dim2=134 mm; Bonnet_dim3=101 mm; Bore=225 mm; Bore1=270 mm; Bore2=360 mm; Centre_D=90 mm; Centre_D1=72 mm; Centre_nut=68 mm; Control_dim1=20 mm  [stored 0.0656168 ft]; Control_dim2=121 mm; Control_dim3=10 mm  [stored 0.0328084 ft]; Control_dim4=346 mm; Control_dim5=27 mm; Control_dim6=33 mm; Control_dim7=59 mm; D=320 mm; DN=450 mm; FL_T=30 mm  [stored 0.0984252 ft]; H3=986 mm; H33=123 mm; H4=247 mm; L=1200 mm; L3=444 mm; Nut_Dim1=51 mm; Nut_Dim2=8 mm  [stored 0.0262467 ft]; Nut_T=24 mm  [stored 0.0787402 ft]; Orifice_FL=269 mm; Raised_R=38 mm; Raised_dis=4 mm  [stored 0.0131234 ft]; Sweep_R=23 mm; Thickness=18 mm  [stored 0.0590551 ft]; Thickness1=22 mm; Total_L=1215 mm; W=383 mm; W1=398 mm; W11=276 mm; W2=398 mm; W22=318 mm; centre=351 mm; dim1=119 mm; nut_dim=192 mm; sweep=36 mm  [stored 0.11811 ft]; sweep/2=8 mm  [stored 0.0262467 ft]; sweep1=15 mm  [stored 0.0492126 ft]; sweep_D=30 mm  [stored 0.0984252 ft]; sweep_H=466 mm; sweep_H1=58 mm; sweep_box1=36 mm  [stored 0.11811 ft]; sweep_box2=20 mm  [stored 0.0656168 ft]; w1=398 mm; w2=398 mm
- DN450_PN16 Flow range ( 445 - 1090): Actuator_L=179 mm; Actuator_L1=161 mm; Actuator_d=50 mm; Body_H=384 mm; Body_Rib_L=160 mm; Bolt_Dia=39 mm  [stored 0.127953 ft]; Bonnet_D=192 mm; Bonnet_D1=384 mm; Bonnet_R=403 mm; Bonnet_dim1=269 mm; Bonnet_dim1_H=41 mm; Bonnet_dim1_H1=536 mm; Bonnet_dim2=134 mm; Bonnet_dim3=101 mm; Bore=225 mm; Bore1=270 mm; Bore2=360 mm; Centre_D=90 mm; Centre_D1=72 mm; Centre_nut=68 mm; Control_dim1=20 mm  [stored 0.0656168 ft]; Control_dim2=121 mm; Control_dim3=10 mm  [stored 0.0328084 ft]; Control_dim4=346 mm; Control_dim5=27 mm; Control_dim6=33 mm; Control_dim7=59 mm; D=320 mm; DN=450 mm; FL_T=30 mm  [stored 0.0984252 ft]; H3=986 mm; H33=123 mm; H4=247 mm; L=1200 mm; L3=444 mm; Nut_Dim1=51 mm; Nut_Dim2=8 mm  [stored 0.0262467 ft]; Nut_T=24 mm  [stored 0.0787402 ft]; Orifice_FL=269 mm; Raised_R=38 mm; Raised_dis=4 mm  [stored 0.0131234 ft]; Sweep_R=23 mm; Thickness=18 mm  [stored 0.0590551 ft]; Thickness1=22 mm; Total_L=1215 mm; W=383 mm; W1=398 mm; W11=276 mm; W2=398 mm; W22=318 mm; centre=351 mm; dim1=119 mm; nut_dim=192 mm; sweep=36 mm  [stored 0.11811 ft]; sweep/2=8 mm  [stored 0.0262467 ft]; sweep1=15 mm  [stored 0.0492126 ft]; sweep_D=30 mm  [stored 0.0984252 ft]; sweep_H=466 mm; sweep_H1=58 mm; sweep_box1=36 mm  [stored 0.11811 ft]; sweep_box2=20 mm  [stored 0.0656168 ft]; w1=398 mm; w2=398 mm
- DN450_PN16 Flow range ( 675 - 1640): Actuator_L=179 mm; Actuator_L1=161 mm; Actuator_d=50 mm; Body_H=384 mm; Body_Rib_L=160 mm; Bolt_Dia=39 mm  [stored 0.127953 ft]; Bonnet_D=192 mm; Bonnet_D1=384 mm; Bonnet_R=403 mm; Bonnet_dim1=269 mm; Bonnet_dim1_H=41 mm; Bonnet_dim1_H1=536 mm; Bonnet_dim2=134 mm; Bonnet_dim3=101 mm; Bore=225 mm; Bore1=270 mm; Bore2=360 mm; Centre_D=90 mm; Centre_D1=72 mm; Centre_nut=68 mm; Control_dim1=20 mm  [stored 0.0656168 ft]; Control_dim2=121 mm; Control_dim3=10 mm  [stored 0.0328084 ft]; Control_dim4=346 mm; Control_dim5=27 mm; Control_dim6=33 mm; Control_dim7=59 mm; D=320 mm; DN=450 mm; FL_T=30 mm  [stored 0.0984252 ft]; H3=986 mm; H33=123 mm; H4=247 mm; L=1200 mm; L3=444 mm; Nut_Dim1=51 mm; Nut_Dim2=8 mm  [stored 0.0262467 ft]; Nut_T=24 mm  [stored 0.0787402 ft]; Orifice_FL=269 mm; Raised_R=38 mm; Raised_dis=4 mm  [stored 0.0131234 ft]; Sweep_R=23 mm; Thickness=18 mm  [stored 0.0590551 ft]; Thickness1=22 mm; Total_L=1215 mm; W=383 mm; W1=398 mm; W11=276 mm; W2=398 mm; W22=318 mm; centre=351 mm; dim1=119 mm; nut_dim=192 mm; sweep=36 mm  [stored 0.11811 ft]; sweep/2=8 mm  [stored 0.0262467 ft]; sweep1=15 mm  [stored 0.0492126 ft]; sweep_D=30 mm  [stored 0.0984252 ft]; sweep_H=466 mm; sweep_H1=58 mm; sweep_box1=36 mm  [stored 0.11811 ft]; sweep_box2=20 mm  [stored 0.0656168 ft]; w1=398 mm; w2=398 mm
- DN450_PN16 Flow range ( 1020 - 2495): Actuator_L=179 mm; Actuator_L1=161 mm; Actuator_d=50 mm; Body_H=384 mm; Body_Rib_L=160 mm; Bolt_Dia=39 mm  [stored 0.127953 ft]; Bonnet_D=192 mm; Bonnet_D1=384 mm; Bonnet_R=403 mm; Bonnet_dim1=269 mm; Bonnet_dim1_H=41 mm; Bonnet_dim1_H1=536 mm; Bonnet_dim2=134 mm; Bonnet_dim3=101 mm; Bore=225 mm; Bore1=270 mm; Bore2=360 mm; Centre_D=90 mm; Centre_D1=72 mm; Centre_nut=68 mm; Control_dim1=20 mm  [stored 0.0656168 ft]; Control_dim2=121 mm; Control_dim3=10 mm  [stored 0.0328084 ft]; Control_dim4=346 mm; Control_dim5=27 mm; Control_dim6=33 mm; Control_dim7=59 mm; D=320 mm; DN=450 mm; FL_T=30 mm  [stored 0.0984252 ft]; H3=986 mm; H33=123 mm; H4=247 mm; L=1200 mm; L3=444 mm; Nut_Dim1=51 mm; Nut_Dim2=8 mm  [stored 0.0262467 ft]; Nut_T=24 mm  [stored 0.0787402 ft]; Orifice_FL=269 mm; Raised_R=38 mm; Raised_dis=4 mm  [stored 0.0131234 ft]; Sweep_R=23 mm; Thickness=18 mm  [stored 0.0590551 ft]; Thickness1=22 mm; Total_L=1215 mm; W=383 mm; W1=398 mm; W11=276 mm; W2=398 mm; W22=318 mm; centre=351 mm; dim1=119 mm; nut_dim=192 mm; sweep=36 mm  [stored 0.11811 ft]; sweep/2=8 mm  [stored 0.0262467 ft]; sweep1=15 mm  [stored 0.0492126 ft]; sweep_D=30 mm  [stored 0.0984252 ft]; sweep_H=466 mm; sweep_H1=58 mm; sweep_box1=36 mm  [stored 0.11811 ft]; sweep_box2=20 mm  [stored 0.0656168 ft]; w1=398 mm; w2=398 mm
- DN500_PN10 Flow range ( 350 - 835): Actuator_L=209 mm; Actuator_L1=188 mm; Actuator_d=56 mm; Body_H=429 mm; Body_Rib_L=179 mm; Bolt_Dia=44 mm; Bonnet_D=215 mm; Bonnet_D1=429 mm; Bonnet_R=450 mm; Bonnet_dim1=300 mm; Bonnet_dim1_H=67 mm; Bonnet_dim1_H1=648 mm; Bonnet_dim2=150 mm; Bonnet_dim3=113 mm; Bore=250 mm; Bore1=300 mm; Bore2=400 mm; Centre_D=100 mm; Centre_D1=80 mm; Centre_nut=75 mm; Control_dim1=23 mm; Control_dim2=135 mm; Control_dim3=11 mm  [stored 0.0360892 ft]; Control_dim4=386 mm; Control_dim5=30 mm  [stored 0.0984252 ft]; Control_dim6=36 mm  [stored 0.11811 ft]; Control_dim7=66 mm; D=358 mm; DN=500 mm; FL_T=32 mm; H3=1163 mm; H33=149 mm; H4=298 mm; L=1250 mm; L3=495 mm; Nut_Dim1=57 mm; Nut_Dim2=9 mm  [stored 0.0295276 ft]; Nut_T=25 mm  [stored 0.082021 ft]; Orifice_FL=296 mm; Raised_R=43 mm; Raised_dis=4 mm  [stored 0.0131234 ft]; Sweep_R=26 mm; Thickness=19 mm  [stored 0.062336 ft]; Thickness1=23 mm; Total_L=1265 mm; W=448 mm; W1=465 mm; W11=323 mm; W2=465 mm; W22=372 mm; centre=390 mm; dim1=140 mm; nut_dim=215 mm; sweep=41 mm; sweep/2=9 mm  [stored 0.0295276 ft]; sweep1=17 mm; sweep_D=34 mm  [stored 0.111549 ft]; sweep_H=564 mm; sweep_H1=94 mm; sweep_box1=40 mm  [stored 0.131234 ft]; sweep_box2=22 mm; w1=465 mm; w2=465 mm
- DN500_PN10 Flow range ( 530 - 1290): Actuator_L=209 mm; Actuator_L1=188 mm; Actuator_d=56 mm; Body_H=429 mm; Body_Rib_L=179 mm; Bolt_Dia=44 mm; Bonnet_D=215 mm; Bonnet_D1=429 mm; Bonnet_R=450 mm; Bonnet_dim1=300 mm; Bonnet_dim1_H=67 mm; Bonnet_dim1_H1=648 mm; Bonnet_dim2=150 mm; Bonnet_dim3=113 mm; Bore=250 mm; Bore1=300 mm; Bore2=400 mm; Centre_D=100 mm; Centre_D1=80 mm; Centre_nut=75 mm; Control_dim1=23 mm; Control_dim2=135 mm; Control_dim3=11 mm  [stored 0.0360892 ft]; Control_dim4=386 mm; Control_dim5=30 mm  [stored 0.0984252 ft]; Control_dim6=36 mm  [stored 0.11811 ft]; Control_dim7=66 mm; D=358 mm; DN=500 mm; FL_T=32 mm; H3=1163 mm; H33=149 mm; H4=298 mm; L=1250 mm; L3=495 mm; Nut_Dim1=57 mm; Nut_Dim2=9 mm  [stored 0.0295276 ft]; Nut_T=25 mm  [stored 0.082021 ft]; Orifice_FL=296 mm; Raised_R=43 mm; Raised_dis=4 mm  [stored 0.0131234 ft]; Sweep_R=26 mm; Thickness=19 mm  [stored 0.062336 ft]; Thickness1=23 mm; Total_L=1265 mm; W=448 mm; W1=465 mm; W11=323 mm; W2=465 mm; W22=372 mm; centre=390 mm; dim1=140 mm; nut_dim=215 mm; sweep=41 mm; sweep/2=9 mm  [stored 0.0295276 ft]; sweep1=17 mm; sweep_D=34 mm  [stored 0.111549 ft]; sweep_H=564 mm; sweep_H1=94 mm; sweep_box1=40 mm  [stored 0.131234 ft]; sweep_box2=22 mm; w1=465 mm; w2=465 mm
- DN500_PN10 Flow range ( 765 - 1860): Actuator_L=209 mm; Actuator_L1=188 mm; Actuator_d=56 mm; Body_H=429 mm; Body_Rib_L=179 mm; Bolt_Dia=44 mm; Bonnet_D=215 mm; Bonnet_D1=429 mm; Bonnet_R=450 mm; Bonnet_dim1=300 mm; Bonnet_dim1_H=67 mm; Bonnet_dim1_H1=648 mm; Bonnet_dim2=150 mm; Bonnet_dim3=113 mm; Bore=250 mm; Bore1=300 mm; Bore2=400 mm; Centre_D=100 mm; Centre_D1=80 mm; Centre_nut=75 mm; Control_dim1=23 mm; Control_dim2=135 mm; Control_dim3=11 mm  [stored 0.0360892 ft]; Control_dim4=386 mm; Control_dim5=30 mm  [stored 0.0984252 ft]; Control_dim6=36 mm  [stored 0.11811 ft]; Control_dim7=66 mm; D=358 mm; DN=500 mm; FL_T=32 mm; H3=1163 mm; H33=149 mm; H4=298 mm; L=1250 mm; L3=495 mm; Nut_Dim1=57 mm; Nut_Dim2=9 mm  [stored 0.0295276 ft]; Nut_T=25 mm  [stored 0.082021 ft]; Orifice_FL=296 mm; Raised_R=43 mm; Raised_dis=4 mm  [stored 0.0131234 ft]; Sweep_R=26 mm; Thickness=19 mm  [stored 0.062336 ft]; Thickness1=23 mm; Total_L=1265 mm; W=448 mm; W1=465 mm; W11=323 mm; W2=465 mm; W22=372 mm; centre=390 mm; dim1=140 mm; nut_dim=215 mm; sweep=41 mm; sweep/2=9 mm  [stored 0.0295276 ft]; sweep1=17 mm; sweep_D=34 mm  [stored 0.111549 ft]; sweep_H=564 mm; sweep_H1=94 mm; sweep_box1=40 mm  [stored 0.131234 ft]; sweep_box2=22 mm; w1=465 mm; w2=465 mm
- DN500_PN10 Flow range ( 1115 - 2715): Actuator_L=209 mm; Actuator_L1=188 mm; Actuator_d=56 mm; Body_H=429 mm; Body_Rib_L=179 mm; Bolt_Dia=44 mm; Bonnet_D=215 mm; Bonnet_D1=429 mm; Bonnet_R=450 mm; Bonnet_dim1=300 mm; Bonnet_dim1_H=67 mm; Bonnet_dim1_H1=648 mm; Bonnet_dim2=150 mm; Bonnet_dim3=113 mm; Bore=250 mm; Bore1=300 mm; Bore2=400 mm; Centre_D=100 mm; Centre_D1=80 mm; Centre_nut=75 mm; Control_dim1=23 mm; Control_dim2=135 mm; Control_dim3=11 mm  [stored 0.0360892 ft]; Control_dim4=386 mm; Control_dim5=30 mm  [stored 0.0984252 ft]; Control_dim6=36 mm  [stored 0.11811 ft]; Control_dim7=66 mm; D=358 mm; DN=500 mm; FL_T=32 mm; H3=1163 mm; H33=149 mm; H4=298 mm; L=1250 mm; L3=495 mm; Nut_Dim1=57 mm; Nut_Dim2=9 mm  [stored 0.0295276 ft]; Nut_T=25 mm  [stored 0.082021 ft]; Orifice_FL=296 mm; Raised_R=43 mm; Raised_dis=4 mm  [stored 0.0131234 ft]; Sweep_R=26 mm; Thickness=19 mm  [stored 0.062336 ft]; Thickness1=23 mm; Total_L=1265 mm; W=448 mm; W1=465 mm; W11=323 mm; W2=465 mm; W22=372 mm; centre=390 mm; dim1=140 mm; nut_dim=215 mm; sweep=41 mm; sweep/2=9 mm  [stored 0.0295276 ft]; sweep1=17 mm; sweep_D=34 mm  [stored 0.111549 ft]; sweep_H=564 mm; sweep_H1=94 mm; sweep_box1=40 mm  [stored 0.131234 ft]; sweep_box2=22 mm; w1=465 mm; w2=465 mm
- DN500_PN16 Flow range ( 350 - 835): Actuator_L=209 mm; Actuator_L1=188 mm; Actuator_d=56 mm; Body_H=429 mm; Body_Rib_L=179 mm; Bolt_Dia=44 mm; Bonnet_D=215 mm; Bonnet_D1=429 mm; Bonnet_R=450 mm; Bonnet_dim1=300 mm; Bonnet_dim1_H=67 mm; Bonnet_dim1_H1=648 mm; Bonnet_dim2=150 mm; Bonnet_dim3=113 mm; Bore=250 mm; Bore1=300 mm; Bore2=400 mm; Centre_D=100 mm; Centre_D1=80 mm; Centre_nut=75 mm; Control_dim1=23 mm; Control_dim2=135 mm; Control_dim3=11 mm  [stored 0.0360892 ft]; Control_dim4=386 mm; Control_dim5=30 mm  [stored 0.0984252 ft]; Control_dim6=36 mm  [stored 0.11811 ft]; Control_dim7=66 mm; D=358 mm; DN=500 mm; FL_T=32 mm; H3=1163 mm; H33=149 mm; H4=298 mm; L=1250 mm; L3=495 mm; Nut_Dim1=57 mm; Nut_Dim2=9 mm  [stored 0.0295276 ft]; Nut_T=25 mm  [stored 0.082021 ft]; Orifice_FL=296 mm; Raised_R=43 mm; Raised_dis=4 mm  [stored 0.0131234 ft]; Sweep_R=26 mm; Thickness=19 mm  [stored 0.062336 ft]; Thickness1=23 mm; Total_L=1265 mm; W=448 mm; W1=465 mm; W11=323 mm; W2=465 mm; W22=372 mm; centre=390 mm; dim1=140 mm; nut_dim=215 mm; sweep=41 mm; sweep/2=9 mm  [stored 0.0295276 ft]; sweep1=17 mm; sweep_D=34 mm  [stored 0.111549 ft]; sweep_H=564 mm; sweep_H1=94 mm; sweep_box1=40 mm  [stored 0.131234 ft]; sweep_box2=22 mm; w1=465 mm; w2=465 mm
- DN500_PN16 Flow range ( 530 - 1290): Actuator_L=209 mm; Actuator_L1=188 mm; Actuator_d=56 mm; Body_H=429 mm; Body_Rib_L=179 mm; Bolt_Dia=44 mm; Bonnet_D=215 mm; Bonnet_D1=429 mm; Bonnet_R=450 mm; Bonnet_dim1=300 mm; Bonnet_dim1_H=67 mm; Bonnet_dim1_H1=648 mm; Bonnet_dim2=150 mm; Bonnet_dim3=113 mm; Bore=250 mm; Bore1=300 mm; Bore2=400 mm; Centre_D=100 mm; Centre_D1=80 mm; Centre_nut=75 mm; Control_dim1=23 mm; Control_dim2=135 mm; Control_dim3=11 mm  [stored 0.0360892 ft]; Control_dim4=386 mm; Control_dim5=30 mm  [stored 0.0984252 ft]; Control_dim6=36 mm  [stored 0.11811 ft]; Control_dim7=66 mm; D=358 mm; DN=500 mm; FL_T=32 mm; H3=1163 mm; H33=149 mm; H4=298 mm; L=1250 mm; L3=495 mm; Nut_Dim1=57 mm; Nut_Dim2=9 mm  [stored 0.0295276 ft]; Nut_T=25 mm  [stored 0.082021 ft]; Orifice_FL=296 mm; Raised_R=43 mm; Raised_dis=4 mm  [stored 0.0131234 ft]; Sweep_R=26 mm; Thickness=19 mm  [stored 0.062336 ft]; Thickness1=23 mm; Total_L=1265 mm; W=448 mm; W1=465 mm; W11=323 mm; W2=465 mm; W22=372 mm; centre=390 mm; dim1=140 mm; nut_dim=215 mm; sweep=41 mm; sweep/2=9 mm  [stored 0.0295276 ft]; sweep1=17 mm; sweep_D=34 mm  [stored 0.111549 ft]; sweep_H=564 mm; sweep_H1=94 mm; sweep_box1=40 mm  [stored 0.131234 ft]; sweep_box2=22 mm; w1=465 mm; w2=465 mm
- DN500_PN16 Flow range ( 765 - 1860): Actuator_L=209 mm; Actuator_L1=188 mm; Actuator_d=56 mm; Body_H=429 mm; Body_Rib_L=179 mm; Bolt_Dia=44 mm; Bonnet_D=215 mm; Bonnet_D1=429 mm; Bonnet_R=450 mm; Bonnet_dim1=300 mm; Bonnet_dim1_H=67 mm; Bonnet_dim1_H1=648 mm; Bonnet_dim2=150 mm; Bonnet_dim3=113 mm; Bore=250 mm; Bore1=300 mm; Bore2=400 mm; Centre_D=100 mm; Centre_D1=80 mm; Centre_nut=75 mm; Control_dim1=23 mm; Control_dim2=135 mm; Control_dim3=11 mm  [stored 0.0360892 ft]; Control_dim4=386 mm; Control_dim5=30 mm  [stored 0.0984252 ft]; Control_dim6=36 mm  [stored 0.11811 ft]; Control_dim7=66 mm; D=358 mm; DN=500 mm; FL_T=32 mm; H3=1163 mm; H33=149 mm; H4=298 mm; L=1250 mm; L3=495 mm; Nut_Dim1=57 mm; Nut_Dim2=9 mm  [stored 0.0295276 ft]; Nut_T=25 mm  [stored 0.082021 ft]; Orifice_FL=296 mm; Raised_R=43 mm; Raised_dis=4 mm  [stored 0.0131234 ft]; Sweep_R=26 mm; Thickness=19 mm  [stored 0.062336 ft]; Thickness1=23 mm; Total_L=1265 mm; W=448 mm; W1=465 mm; W11=323 mm; W2=465 mm; W22=372 mm; centre=390 mm; dim1=140 mm; nut_dim=215 mm; sweep=41 mm; sweep/2=9 mm  [stored 0.0295276 ft]; sweep1=17 mm; sweep_D=34 mm  [stored 0.111549 ft]; sweep_H=564 mm; sweep_H1=94 mm; sweep_box1=40 mm  [stored 0.131234 ft]; sweep_box2=22 mm; w1=465 mm; w2=465 mm
- DN500_PN16 Flow range ( 1115 - 2715): Actuator_L=209 mm; Actuator_L1=188 mm; Actuator_d=56 mm; Body_H=429 mm; Body_Rib_L=179 mm; Bolt_Dia=44 mm; Bonnet_D=215 mm; Bonnet_D1=429 mm; Bonnet_R=450 mm; Bonnet_dim1=300 mm; Bonnet_dim1_H=67 mm; Bonnet_dim1_H1=648 mm; Bonnet_dim2=150 mm; Bonnet_dim3=113 mm; Bore=250 mm; Bore1=300 mm; Bore2=400 mm; Centre_D=100 mm; Centre_D1=80 mm; Centre_nut=75 mm; Control_dim1=23 mm; Control_dim2=135 mm; Control_dim3=11 mm  [stored 0.0360892 ft]; Control_dim4=386 mm; Control_dim5=30 mm  [stored 0.0984252 ft]; Control_dim6=36 mm  [stored 0.11811 ft]; Control_dim7=66 mm; D=358 mm; DN=500 mm; FL_T=32 mm; H3=1163 mm; H33=149 mm; H4=298 mm; L=1250 mm; L3=495 mm; Nut_Dim1=57 mm; Nut_Dim2=9 mm  [stored 0.0295276 ft]; Nut_T=25 mm  [stored 0.082021 ft]; Orifice_FL=296 mm; Raised_R=43 mm; Raised_dis=4 mm  [stored 0.0131234 ft]; Sweep_R=26 mm; Thickness=19 mm  [stored 0.062336 ft]; Thickness1=23 mm; Total_L=1265 mm; W=448 mm; W1=465 mm; W11=323 mm; W2=465 mm; W22=372 mm; centre=390 mm; dim1=140 mm; nut_dim=215 mm; sweep=41 mm; sweep/2=9 mm  [stored 0.0295276 ft]; sweep1=17 mm; sweep_D=34 mm  [stored 0.111549 ft]; sweep_H=564 mm; sweep_H1=94 mm; sweep_box1=40 mm  [stored 0.131234 ft]; sweep_box2=22 mm; w1=465 mm; w2=465 mm
- DN600_PN10 Flow range ( 500 - 1225): Actuator_L=229 mm; Actuator_L1=206 mm; Actuator_d=66 mm; Body_H=504 mm; Body_Rib_L=210 mm; Bolt_Dia=44 mm; Bonnet_D=252 mm; Bonnet_D1=504 mm; Bonnet_R=529 mm; Bonnet_dim1=353 mm; Bonnet_dim1_H=46 mm; Bonnet_dim1_H1=686 mm; Bonnet_dim2=176 mm; Bonnet_dim3=132 mm; Bore=300 mm; Bore1=360 mm; Bore2=480 mm; Centre_D=100 mm; Centre_D1=80 mm; Centre_nut=75 mm; Control_dim1=26 mm; Control_dim2=159 mm; Control_dim3=13 mm  [stored 0.0426509 ft]; Control_dim4=454 mm; Control_dim5=36 mm  [stored 0.11811 ft]; Control_dim6=43 mm; Control_dim7=77 mm; D=420 mm; DN=600 mm; FL_T=36 mm  [stored 0.11811 ft]; H3=1272 mm; H33=158 mm; H4=316 mm; L=1450 mm; L3=582 mm; Nut_Dim1=57 mm; Nut_Dim2=11 mm  [stored 0.0360892 ft]; Nut_T=29 mm; Orifice_FL=347 mm; Raised_R=48 mm; Raised_dis=5 mm  [stored 0.0164042 ft]; Sweep_R=26 mm; Thickness=22 mm; Thickness1=26 mm; Total_L=1465 mm; W=492 mm; W1=509 mm; W11=356 mm; W2=509 mm; W22=407 mm; centre=468 mm; dim1=153 mm; nut_dim=252 mm; sweep=41 mm; sweep/2=9 mm  [stored 0.0295276 ft]; sweep1=17 mm; sweep_D=34 mm  [stored 0.111549 ft]; sweep_H=596 mm; sweep_H1=65 mm; sweep_box1=40 mm  [stored 0.131234 ft]; sweep_box2=22 mm; w1=509 mm; w2=509 mm
- DN600_PN10 Flow range ( 710 - 1735): Actuator_L=229 mm; Actuator_L1=206 mm; Actuator_d=66 mm; Body_H=504 mm; Body_Rib_L=210 mm; Bolt_Dia=44 mm; Bonnet_D=252 mm; Bonnet_D1=504 mm; Bonnet_R=529 mm; Bonnet_dim1=353 mm; Bonnet_dim1_H=46 mm; Bonnet_dim1_H1=686 mm; Bonnet_dim2=176 mm; Bonnet_dim3=132 mm; Bore=300 mm; Bore1=360 mm; Bore2=480 mm; Centre_D=100 mm; Centre_D1=80 mm; Centre_nut=75 mm; Control_dim1=26 mm; Control_dim2=159 mm; Control_dim3=13 mm  [stored 0.0426509 ft]; Control_dim4=454 mm; Control_dim5=36 mm  [stored 0.11811 ft]; Control_dim6=43 mm; Control_dim7=77 mm; D=420 mm; DN=600 mm; FL_T=36 mm  [stored 0.11811 ft]; H3=1272 mm; H33=158 mm; H4=316 mm; L=1450 mm; L3=582 mm; Nut_Dim1=57 mm; Nut_Dim2=11 mm  [stored 0.0360892 ft]; Nut_T=29 mm; Orifice_FL=347 mm; Raised_R=48 mm; Raised_dis=5 mm  [stored 0.0164042 ft]; Sweep_R=26 mm; Thickness=22 mm; Thickness1=26 mm; Total_L=1465 mm; W=492 mm; W1=509 mm; W11=356 mm; W2=509 mm; W22=407 mm; centre=468 mm; dim1=153 mm; nut_dim=252 mm; sweep=41 mm; sweep/2=9 mm  [stored 0.0295276 ft]; sweep1=17 mm; sweep_D=34 mm  [stored 0.111549 ft]; sweep_H=596 mm; sweep_H1=65 mm; sweep_box1=40 mm  [stored 0.131234 ft]; sweep_box2=22 mm; w1=509 mm; w2=509 mm
- DN600_PN10 Flow range ( 970 - 2360): Actuator_L=229 mm; Actuator_L1=206 mm; Actuator_d=66 mm; Body_H=504 mm; Body_Rib_L=210 mm; Bolt_Dia=44 mm; Bonnet_D=252 mm; Bonnet_D1=504 mm; Bonnet_R=529 mm; Bonnet_dim1=353 mm; Bonnet_dim1_H=46 mm; Bonnet_dim1_H1=686 mm; Bonnet_dim2=176 mm; Bonnet_dim3=132 mm; Bore=300 mm; Bore1=360 mm; Bore2=480 mm; Centre_D=100 mm; Centre_D1=80 mm; Centre_nut=75 mm; Control_dim1=26 mm; Control_dim2=159 mm; Control_dim3=13 mm  [stored 0.0426509 ft]; Control_dim4=454 mm; Control_dim5=36 mm  [stored 0.11811 ft]; Control_dim6=43 mm; Control_dim7=77 mm; D=420 mm; DN=600 mm; FL_T=36 mm  [stored 0.11811 ft]; H3=1272 mm; H33=158 mm; H4=316 mm; L=1450 mm; L3=582 mm; Nut_Dim1=57 mm; Nut_Dim2=11 mm  [stored 0.0360892 ft]; Nut_T=29 mm; Orifice_FL=347 mm; Raised_R=48 mm; Raised_dis=5 mm  [stored 0.0164042 ft]; Sweep_R=26 mm; Thickness=22 mm; Thickness1=26 mm; Total_L=1465 mm; W=492 mm; W1=509 mm; W11=356 mm; W2=509 mm; W22=407 mm; centre=468 mm; dim1=153 mm; nut_dim=252 mm; sweep=41 mm; sweep/2=9 mm  [stored 0.0295276 ft]; sweep1=17 mm; sweep_D=34 mm  [stored 0.111549 ft]; sweep_H=596 mm; sweep_H1=65 mm; sweep_box1=40 mm  [stored 0.131234 ft]; sweep_box2=22 mm; w1=509 mm; w2=509 mm
- DN600_PN10 Flow range ( 1780 - 4350): Actuator_L=229 mm; Actuator_L1=206 mm; Actuator_d=66 mm; Body_H=504 mm; Body_Rib_L=210 mm; Bolt_Dia=44 mm; Bonnet_D=252 mm; Bonnet_D1=504 mm; Bonnet_R=529 mm; Bonnet_dim1=353 mm; Bonnet_dim1_H=46 mm; Bonnet_dim1_H1=686 mm; Bonnet_dim2=176 mm; Bonnet_dim3=132 mm; Bore=300 mm; Bore1=360 mm; Bore2=480 mm; Centre_D=100 mm; Centre_D1=80 mm; Centre_nut=75 mm; Control_dim1=26 mm; Control_dim2=159 mm; Control_dim3=13 mm  [stored 0.0426509 ft]; Control_dim4=454 mm; Control_dim5=36 mm  [stored 0.11811 ft]; Control_dim6=43 mm; Control_dim7=77 mm; D=420 mm; DN=600 mm; FL_T=36 mm  [stored 0.11811 ft]; H3=1272 mm; H33=158 mm; H4=316 mm; L=1450 mm; L3=582 mm; Nut_Dim1=57 mm; Nut_Dim2=11 mm  [stored 0.0360892 ft]; Nut_T=29 mm; Orifice_FL=347 mm; Raised_R=48 mm; Raised_dis=5 mm  [stored 0.0164042 ft]; Sweep_R=26 mm; Thickness=22 mm; Thickness1=26 mm; Total_L=1465 mm; W=492 mm; W1=509 mm; W11=356 mm; W2=509 mm; W22=407 mm; centre=468 mm; dim1=153 mm; nut_dim=252 mm; sweep=41 mm; sweep/2=9 mm  [stored 0.0295276 ft]; sweep1=17 mm; sweep_D=34 mm  [stored 0.111549 ft]; sweep_H=596 mm; sweep_H1=65 mm; sweep_box1=40 mm  [stored 0.131234 ft]; sweep_box2=22 mm; w1=509 mm; w2=509 mm
- DN600_PN16 Flow range ( 500 - 1225): Actuator_L=229 mm; Actuator_L1=206 mm; Actuator_d=66 mm; Body_H=504 mm; Body_Rib_L=210 mm; Bolt_Dia=44 mm; Bonnet_D=252 mm; Bonnet_D1=504 mm; Bonnet_R=529 mm; Bonnet_dim1=353 mm; Bonnet_dim1_H=46 mm; Bonnet_dim1_H1=686 mm; Bonnet_dim2=176 mm; Bonnet_dim3=132 mm; Bore=300 mm; Bore1=360 mm; Bore2=480 mm; Centre_D=100 mm; Centre_D1=80 mm; Centre_nut=75 mm; Control_dim1=26 mm; Control_dim2=159 mm; Control_dim3=13 mm  [stored 0.0426509 ft]; Control_dim4=454 mm; Control_dim5=36 mm  [stored 0.11811 ft]; Control_dim6=43 mm; Control_dim7=77 mm; D=420 mm; DN=600 mm; FL_T=36 mm  [stored 0.11811 ft]; H3=1272 mm; H33=158 mm; H4=316 mm; L=1450 mm; L3=582 mm; Nut_Dim1=57 mm; Nut_Dim2=11 mm  [stored 0.0360892 ft]; Nut_T=29 mm; Orifice_FL=347 mm; Raised_R=48 mm; Raised_dis=5 mm  [stored 0.0164042 ft]; Sweep_R=26 mm; Thickness=22 mm; Thickness1=26 mm; Total_L=1465 mm; W=492 mm; W1=509 mm; W11=356 mm; W2=509 mm; W22=407 mm; centre=468 mm; dim1=153 mm; nut_dim=252 mm; sweep=41 mm; sweep/2=9 mm  [stored 0.0295276 ft]; sweep1=17 mm; sweep_D=34 mm  [stored 0.111549 ft]; sweep_H=596 mm; sweep_H1=65 mm; sweep_box1=40 mm  [stored 0.131234 ft]; sweep_box2=22 mm; w1=509 mm; w2=509 mm
- DN600_PN16 Flow range ( 710 - 1735): Actuator_L=229 mm; Actuator_L1=206 mm; Actuator_d=66 mm; Body_H=504 mm; Body_Rib_L=210 mm; Bolt_Dia=44 mm; Bonnet_D=252 mm; Bonnet_D1=504 mm; Bonnet_R=529 mm; Bonnet_dim1=353 mm; Bonnet_dim1_H=46 mm; Bonnet_dim1_H1=686 mm; Bonnet_dim2=176 mm; Bonnet_dim3=132 mm; Bore=300 mm; Bore1=360 mm; Bore2=480 mm; Centre_D=100 mm; Centre_D1=80 mm; Centre_nut=75 mm; Control_dim1=26 mm; Control_dim2=159 mm; Control_dim3=13 mm  [stored 0.0426509 ft]; Control_dim4=454 mm; Control_dim5=36 mm  [stored 0.11811 ft]; Control_dim6=43 mm; Control_dim7=77 mm; D=420 mm; DN=600 mm; FL_T=36 mm  [stored 0.11811 ft]; H3=1272 mm; H33=158 mm; H4=316 mm; L=1450 mm; L3=582 mm; Nut_Dim1=57 mm; Nut_Dim2=11 mm  [stored 0.0360892 ft]; Nut_T=29 mm; Orifice_FL=347 mm; Raised_R=48 mm; Raised_dis=5 mm  [stored 0.0164042 ft]; Sweep_R=26 mm; Thickness=22 mm; Thickness1=26 mm; Total_L=1465 mm; W=492 mm; W1=509 mm; W11=356 mm; W2=509 mm; W22=407 mm; centre=468 mm; dim1=153 mm; nut_dim=252 mm; sweep=41 mm; sweep/2=9 mm  [stored 0.0295276 ft]; sweep1=17 mm; sweep_D=34 mm  [stored 0.111549 ft]; sweep_H=596 mm; sweep_H1=65 mm; sweep_box1=40 mm  [stored 0.131234 ft]; sweep_box2=22 mm; w1=509 mm; w2=509 mm
- DN600_PN16 Flow range ( 970 - 2360): Actuator_L=229 mm; Actuator_L1=206 mm; Actuator_d=66 mm; Body_H=504 mm; Body_Rib_L=210 mm; Bolt_Dia=44 mm; Bonnet_D=252 mm; Bonnet_D1=504 mm; Bonnet_R=529 mm; Bonnet_dim1=353 mm; Bonnet_dim1_H=46 mm; Bonnet_dim1_H1=686 mm; Bonnet_dim2=176 mm; Bonnet_dim3=132 mm; Bore=300 mm; Bore1=360 mm; Bore2=480 mm; Centre_D=100 mm; Centre_D1=80 mm; Centre_nut=75 mm; Control_dim1=26 mm; Control_dim2=159 mm; Control_dim3=13 mm  [stored 0.0426509 ft]; Control_dim4=454 mm; Control_dim5=36 mm  [stored 0.11811 ft]; Control_dim6=43 mm; Control_dim7=77 mm; D=420 mm; DN=600 mm; FL_T=36 mm  [stored 0.11811 ft]; H3=1272 mm; H33=158 mm; H4=316 mm; L=1450 mm; L3=582 mm; Nut_Dim1=57 mm; Nut_Dim2=11 mm  [stored 0.0360892 ft]; Nut_T=29 mm; Orifice_FL=347 mm; Raised_R=48 mm; Raised_dis=5 mm  [stored 0.0164042 ft]; Sweep_R=26 mm; Thickness=22 mm; Thickness1=26 mm; Total_L=1465 mm; W=492 mm; W1=509 mm; W11=356 mm; W2=509 mm; W22=407 mm; centre=468 mm; dim1=153 mm; nut_dim=252 mm; sweep=41 mm; sweep/2=9 mm  [stored 0.0295276 ft]; sweep1=17 mm; sweep_D=34 mm  [stored 0.111549 ft]; sweep_H=596 mm; sweep_H1=65 mm; sweep_box1=40 mm  [stored 0.131234 ft]; sweep_box2=22 mm; w1=509 mm; w2=509 mm
- DN600_PN16 Flow range ( 1780 - 4350): Actuator_L=229 mm; Actuator_L1=206 mm; Actuator_d=66 mm; Body_H=504 mm; Body_Rib_L=210 mm; Bolt_Dia=44 mm; Bonnet_D=252 mm; Bonnet_D1=504 mm; Bonnet_R=529 mm; Bonnet_dim1=353 mm; Bonnet_dim1_H=46 mm; Bonnet_dim1_H1=686 mm; Bonnet_dim2=176 mm; Bonnet_dim3=132 mm; Bore=300 mm; Bore1=360 mm; Bore2=480 mm; Centre_D=100 mm; Centre_D1=80 mm; Centre_nut=75 mm; Control_dim1=26 mm; Control_dim2=159 mm; Control_dim3=13 mm  [stored 0.0426509 ft]; Control_dim4=454 mm; Control_dim5=36 mm  [stored 0.11811 ft]; Control_dim6=43 mm; Control_dim7=77 mm; D=420 mm; DN=600 mm; FL_T=36 mm  [stored 0.11811 ft]; H3=1272 mm; H33=158 mm; H4=316 mm; L=1450 mm; L3=582 mm; Nut_Dim1=57 mm; Nut_Dim2=11 mm  [stored 0.0360892 ft]; Nut_T=29 mm; Orifice_FL=347 mm; Raised_R=48 mm; Raised_dis=5 mm  [stored 0.0164042 ft]; Sweep_R=26 mm; Thickness=22 mm; Thickness1=26 mm; Total_L=1465 mm; W=492 mm; W1=509 mm; W11=356 mm; W2=509 mm; W22=407 mm; centre=468 mm; dim1=153 mm; nut_dim=252 mm; sweep=41 mm; sweep/2=9 mm  [stored 0.0295276 ft]; sweep1=17 mm; sweep_D=34 mm  [stored 0.111549 ft]; sweep_H=596 mm; sweep_H1=65 mm; sweep_box1=40 mm  [stored 0.131234 ft]; sweep_box2=22 mm; w1=509 mm; w2=509 mm

note: [stored X ft] marks values corroborated as IEEE doubles in the binary element streams (Revit-internal decimal feet)

## geometry (parser evidence)
native form markers: Sweep x6
no freeform markers — native parametric forms only
